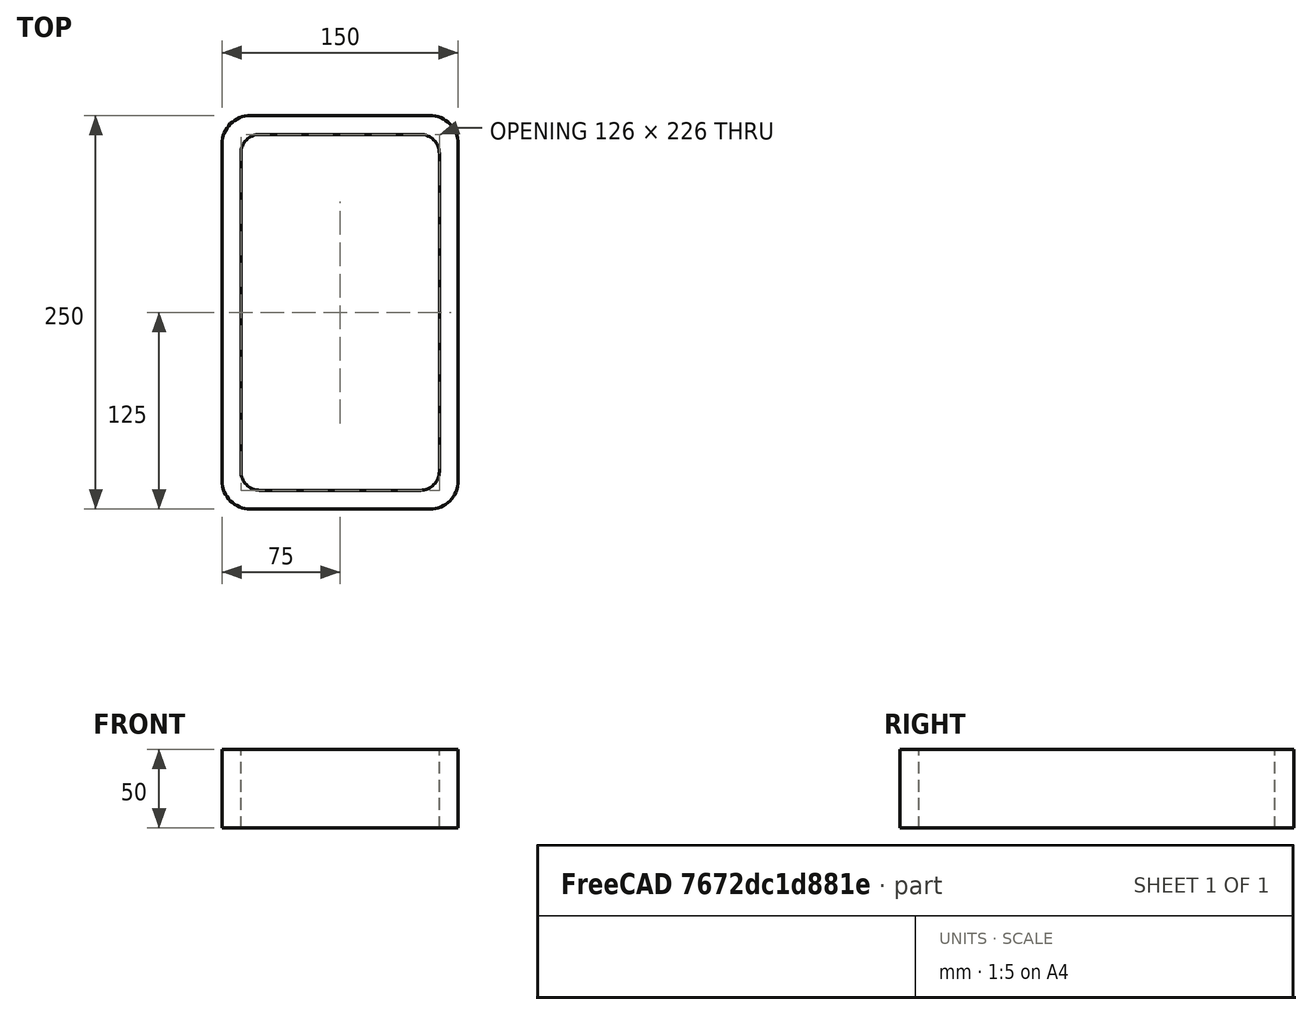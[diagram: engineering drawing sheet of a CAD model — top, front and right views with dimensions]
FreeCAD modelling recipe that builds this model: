
FCSTD DOCUMENT  (FreeCAD 0.15R4671 (Git))
Label: Rectangular hollow section 250x150x12 EN10219 S235JRH
License: All rights reserved
LicenseURL: http://en.wikipedia.org/wiki/All_rights_reserved
objects: Sketcher::SketchObject×1, Part::Extrusion×1
note: 2 computed .brp shape members not serialized (recipe doc carries the construction recipe); baked Part::Feature solids carry a one-line shape summary decoded from their .brp

FEATURE [Sketcher::SketchObject] Sketch
  sketch-geometry (16):
    g0: LineSegment StartX=-51 StartY=113 StartZ=0 EndX=51 EndY=113 EndZ=0
    g1: LineSegment StartX=63 StartY=101 StartZ=0 EndX=63 EndY=-101 EndZ=0
    g2: LineSegment StartX=51 StartY=-113 StartZ=0 EndX=-51 EndY=-113 EndZ=0
    g3: LineSegment StartX=-63 StartY=-101 StartZ=0 EndX=-63 EndY=101 EndZ=0
    g4: LineSegment StartX=-57 StartY=125 StartZ=0 EndX=57 EndY=125 EndZ=0
    g5: LineSegment StartX=75 StartY=107 StartZ=0 EndX=75 EndY=-107 EndZ=0
    g6: LineSegment StartX=57 StartY=-125 StartZ=0 EndX=-57 EndY=-125 EndZ=0
    g7: LineSegment StartX=-75 StartY=-107 StartZ=0 EndX=-75 EndY=107 EndZ=0
    g8: ArcOfCircle CenterX=-51 CenterY=101 CenterZ=0 NormalX=0 NormalY=0 NormalZ=1 Radius=12 StartAngle=1.5708 EndAngle=3.14159
    g9: ArcOfCircle CenterX=51 CenterY=101 CenterZ=0 NormalX=0 NormalY=0 NormalZ=1 Radius=12 StartAngle=0 EndAngle=1.5708
    g10: ArcOfCircle CenterX=51 CenterY=-101 CenterZ=0 NormalX=0 NormalY=0 NormalZ=1 Radius=12 StartAngle=4.71239 EndAngle=6.28319
    g11: ArcOfCircle CenterX=-51 CenterY=-101 CenterZ=0 NormalX=0 NormalY=0 NormalZ=1 Radius=12 StartAngle=3.14159 EndAngle=4.71239
    g12: ArcOfCircle CenterX=57 CenterY=107 CenterZ=0 NormalX=0 NormalY=0 NormalZ=1 Radius=18 StartAngle=0 EndAngle=1.5708
    g13: ArcOfCircle CenterX=57 CenterY=-107 CenterZ=0 NormalX=0 NormalY=0 NormalZ=1 Radius=18 StartAngle=4.71239 EndAngle=6.28319
    g14: ArcOfCircle CenterX=-57 CenterY=-107 CenterZ=0 NormalX=0 NormalY=0 NormalZ=1 Radius=18 StartAngle=3.14159 EndAngle=4.71239
    g15: ArcOfCircle CenterX=-57 CenterY=107 CenterZ=0 NormalX=0 NormalY=0 NormalZ=1 Radius=18 StartAngle=1.5708 EndAngle=3.14159
  constraints (36):
    c: Horizontal(g2)
    c: Vertical(g3)
    c: Horizontal(g6)
    c: Vertical(g7)
    c: Tangent(g3,g8) = 1.5708
    c: Tangent(g0,g8) = 1.5708
    c: Tangent(g0,g9) = 1.5708
    c: Tangent(g1,g9) = 1.5708
    c: Tangent(g1,g10) = 1.5708
    c: Tangent(g2,g10) = 1.5708
    c: Tangent(g2,g11) = 1.5708
    c: Tangent(g3,g11) = 1.5708
    c: Tangent(g4,g12) = 1.5708
    c: Tangent(g5,g12) = 1.5708
    c: Tangent(g5,g13) = 1.5708
    c: Tangent(g6,g13) = 1.5708
    c: Tangent(g6,g14) = 1.5708
    c: Tangent(g7,g14) = 1.5708
    c: Tangent(g7,g15) = 1.5708
    c: Tangent(g4,g15) = 1.5708
    c: Equal(g9,g8)
    c: Equal(g9,g11)
    c: Equal(g9,g10)
    c: Equal(g12,g15)
    c: Equal(g12,g14)
    c: Equal(g12,g13)
    c: Symmetric(g4,g6,g-1)
    c: Symmetric(g7,g5,g-2)
    c: DistanceY(g4,g6) = -250
    c: DistanceX(g7,g5) = 150
    c: Symmetric(g3,g1,g-2)
    c: Symmetric(g0,g2,g-1)
    c: DistanceY(g0,g4) = 12
    c: DistanceX(g5,g1) = -12
    c: Radius(g9) = 12
    c: Radius(g12) = 18
FEATURE [Part::Extrusion] Extrude  label="Rectangular hollow section 250x150x12 EN10219 S235JRH"
  Base = -> Sketch
  Dir = (0,0,50)
  Solid = true
